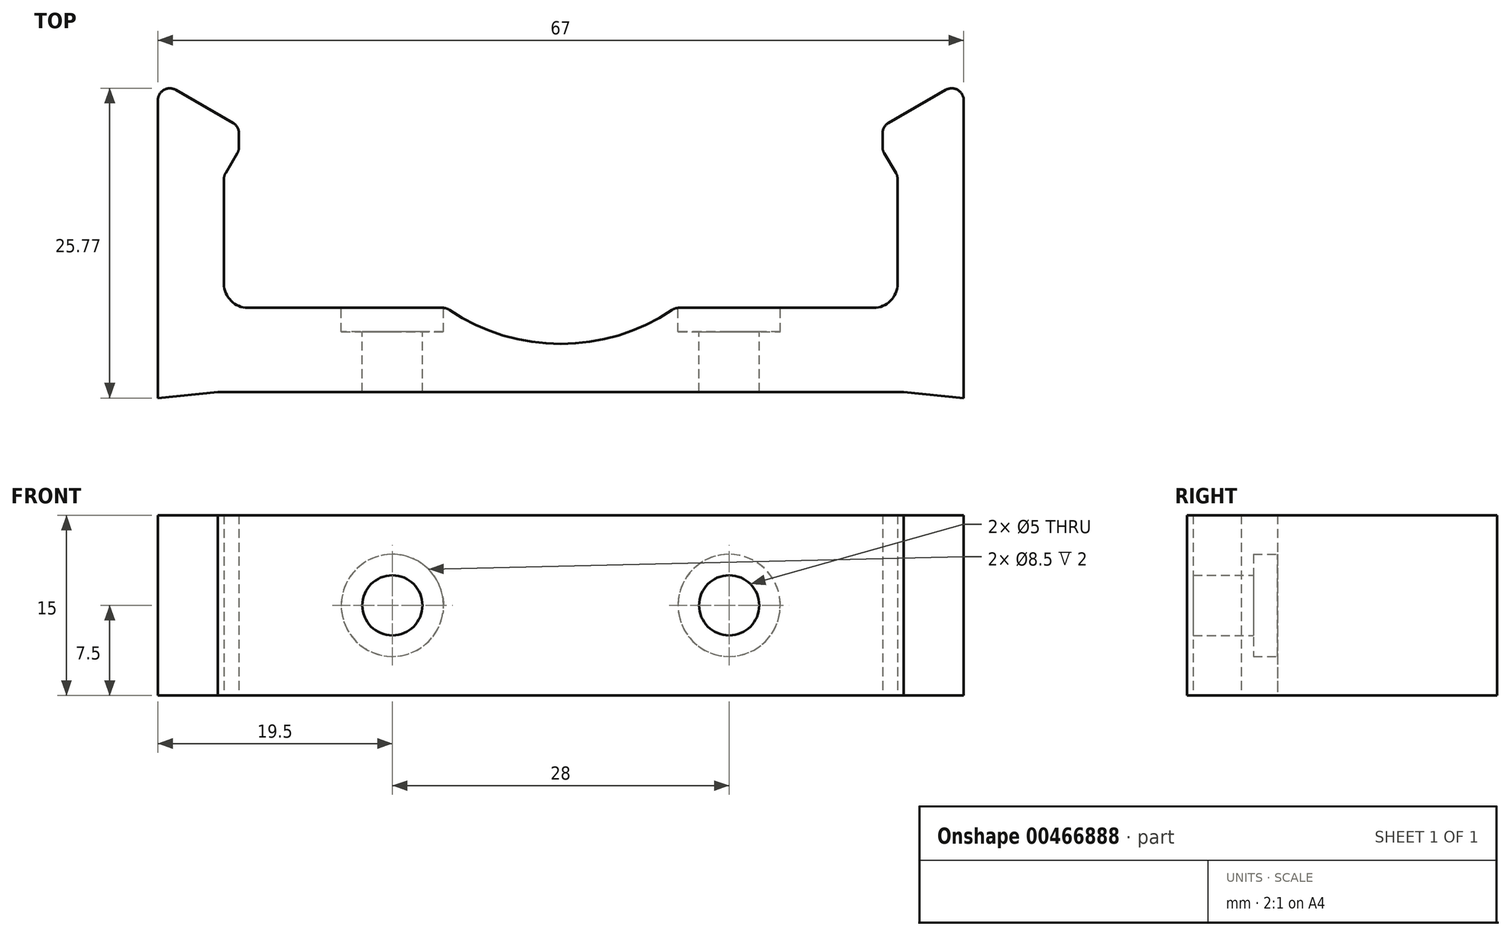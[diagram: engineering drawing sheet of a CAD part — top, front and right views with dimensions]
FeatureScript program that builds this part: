
annotation { "Feature Type Name" : "Feature", "Feature Type Description" : "" }
export const myFeature = defineFeature(function(context is Context, id is Id, definition is map)
    precondition{}
    {
        {
            var Q0;
            Q0=qCreatedBy(makeId("Top.planeOp"),FACE);
            var sketch = newSketch(context, id + "F0", { "sketchPlane" : qUnion([Q0])});
            skLineSegment(sketch, "E0.bottom", {"start": v(-33.5, -13) * mm, "end": v(33.5, -13) * mm});
            skLineSegment(sketch, "E0.top", {"start": v(-33.5, 13) * mm, "end": v(33.5, 13) * mm});
            skLineSegment(sketch, "E0.left", {"start": v(-33.5, -13) * mm, "end": v(-33.5, 13) * mm});
            skLineSegment(sketch, "E0.right", {"start": v(33.5, -13) * mm, "end": v(33.5, 13) * mm});
            skPoint(sketch, "E0.middle", {"position": v(0, 0) * mm});
            skLineSegment(sketch, "E1", {"start": v(-33.5, 13) * mm, "end": v(-26.75, 9.1) * mm});
            skLineSegment(sketch, "E2", {"start": v(-26.75, 9.1) * mm, "end": v(-26.75, 7.1) * mm});
            skLineSegment(sketch, "E3", {"start": v(-26.75, 7.1) * mm, "end": v(-28, 5) * mm});
            skLineSegment(sketch, "E4", {"start": v(-28, 5) * mm, "end": v(-28, -6) * mm});
            skLineSegment(sketch, "E5", {"start": v(-28, -6) * mm, "end": v(-9.5, -6) * mm});
            skArc(sketch, "E6", {"start": v(-9.5, -6) * mm, "mid": v(-4.98, -8.23) * mm, "end": v(0, -9) * mm});
            skLineSegment(sketch, "E7", {"start": v(0, 13) * mm, "end": v(0, -13) * mm, "construction": true});
            skLineSegment(sketch, "E8", {"start": v(0, -13) * mm, "end": v(0, -9) * mm});
            skPoint(sketch, "E9.orphan", {"position": v(9.5, -6) * mm});
            skLineSegment(sketch, "E10", {"start": v(-33.5, -13) * mm, "end": v(-33.5, -13.5) * mm});
            skLineSegment(sketch, "E11", {"start": v(-33.5, -13.5) * mm, "end": v(-28.5, -13) * mm});
            skSolve(sketch);
        }
        {
            var Q0;
            {var subQ0=sQuery(id+"F0.wireOp",EDGE,"E0.left");Q0=makeQuery(id+"F0.imprint","IMPRINT",FACE,{"disambiguationData":[TD([[makeQuery(id+"F0.imprint","IMPRINT",EDGE,{"derivedFrom":subQ0}),-1.0]])]});}
            var Q1;
            {var subQ0=sQuery(id+"F0.wireOp",EDGE,"E10");Q1=makeQuery(id+"F0.imprint","IMPRINT",FACE,{"disambiguationData":[TD([[makeQuery(id+"F0.imprint","IMPRINT",EDGE,{"derivedFrom":subQ0}),1.0]])]});}
            extrude(context, id + "F1", {"entities" : qUnion([Q0, Q1]), "endBound" : BoundingType.SYMMETRIC, "depth" : 15 * mm});
        }
        {
            var Q0;
            Q0=makeQuery(id+"F1.opExtrude","SWEPT_FACE",FACE,{"disambiguationData":[OSD([sQuery(id+"F0.wireOp",EDGE,"E5")])]});
            var sketch = newSketch(context, id + "F2", { "sketchPlane" : qUnion([Q0])});
            skPoint(sketch, "E12", {"position": v(14, 0) * mm});
            skSolve(sketch);
        }
        {
            var Q0;
            Q0=sQuery(id+"F2.wireOp",VERTEX,"E12");
            var Q1;
            Q1=makeQuery(id+"F1.opExtrude","SWEPT_BODY",BODY,{"disambiguationData":[OSD([sQuery(id+"F0.wireOp",EDGE,"E0.bottom"),sQuery(id+"F0.wireOp",EDGE,"E0.left"),sQuery(id+"F0.wireOp",EDGE,"E1"),sQuery(id+"F0.wireOp",EDGE,"E2"),sQuery(id+"F0.wireOp",EDGE,"E3"),sQuery(id+"F0.wireOp",EDGE,"E4"),sQuery(id+"F0.wireOp",EDGE,"E5"),sQuery(id+"F0.wireOp",EDGE,"E6"),sQuery(id+"F0.wireOp",EDGE,"E8")])]});
            hole(context, id + "F3", {"style" : HoleStyle.C_BORE, "endStyle" : HoleEndStyle.THROUGH, "standardTappedOrClearance" : lookupTablePath({ "standard" : "ISO", "size" : "5", "type" : "Drilled" }), "standardBlindInLast" : lookupTablePath({ "standard" : "ISO", "size" : "5", "type" : "Drilled" }), "holeDiameter" : 5 * mm, "cBoreDiameter" : 8.5 * mm, "cBoreDepth" : 2 * mm, "isTappedThrough" : true, "tappedDepth" : 12 * mm, "tapClearance" : 3, "locations" : qUnion([Q0]), "scope" : qUnion([Q1])});
        }
        {
            var Q0;
            Q0=makeQuery(id+"F1.opExtrude","SWEPT_EDGE",EDGE,{"disambiguationData":[OSD([sQuery(id+"F0.wireOp",EDGE,"E5"),sQuery(id+"F0.wireOp",EDGE,"E6")])]});
            var Q1;
            Q1=makeQuery(id+"F1.opExtrude","SWEPT_EDGE",EDGE,{"disambiguationData":[OSD([sQuery(id+"F0.wireOp",EDGE,"E3"),sQuery(id+"F0.wireOp",EDGE,"E4")])]});
            var Q2;
            Q2=makeQuery(id+"F1.opExtrude","SWEPT_EDGE",EDGE,{"disambiguationData":[OSD([sQuery(id+"F0.wireOp",EDGE,"E2"),sQuery(id+"F0.wireOp",EDGE,"E3")])]});
            var Q3;
            Q3=makeQuery(id+"F1.opExtrude","SWEPT_EDGE",EDGE,{"disambiguationData":[OSD([sQuery(id+"F0.wireOp",EDGE,"E1"),sQuery(id+"F0.wireOp",EDGE,"E2")])]});
            var Q4;
            Q4=makeQuery(id+"F1.opExtrude","SWEPT_EDGE",EDGE,{"disambiguationData":[OSD([sQuery(id+"F0.wireOp",EDGE,"E0.top"),sQuery(id+"F0.wireOp",EDGE,"E0.left"),sQuery(id+"F0.wireOp",EDGE,"E1")])]});
            fillet(context, id + "F4", {"entities" : qUnion([Q0, Q1, Q2, Q3, Q4]), "radius" : 1 * mm, "tangentPropagation" : true, "allowEdgeOverflow" : false});
        }
        {
            var Q0;
            Q0=makeQuery(id+"F1.opExtrude","SWEPT_EDGE",EDGE,{"disambiguationData":[OSD([sQuery(id+"F0.wireOp",EDGE,"E4"),sQuery(id+"F0.wireOp",EDGE,"E5")])]});
            fillet(context, id + "F5", {"entities" : qUnion([Q0]), "radius" : 2 * mm, "tangentPropagation" : true, "allowEdgeOverflow" : false});
        }
        {
            var Q0;
            Q0=makeQuery(id+"F1.opExtrude","SWEPT_BODY",BODY,{"disambiguationData":[OSD([sQuery(id+"F0.wireOp",EDGE,"E0.bottom"),sQuery(id+"F0.wireOp",EDGE,"E0.left"),sQuery(id+"F0.wireOp",EDGE,"E1"),sQuery(id+"F0.wireOp",EDGE,"E2"),sQuery(id+"F0.wireOp",EDGE,"E3"),sQuery(id+"F0.wireOp",EDGE,"E4"),sQuery(id+"F0.wireOp",EDGE,"E5"),sQuery(id+"F0.wireOp",EDGE,"E6"),sQuery(id+"F0.wireOp",EDGE,"E8")])]});
            var Q1;
            Q1=makeQuery(id+"F1.opExtrude","SWEPT_FACE",FACE,{"disambiguationData":[OSD([sQuery(id+"F0.wireOp",EDGE,"E8")])]});
            mirror(context, id + "F6", {"operationType" : NewBodyOperationType.ADD, "entities" : qUnion([Q0]), "mirrorPlane" : qUnion([Q1])});
        }
    });
